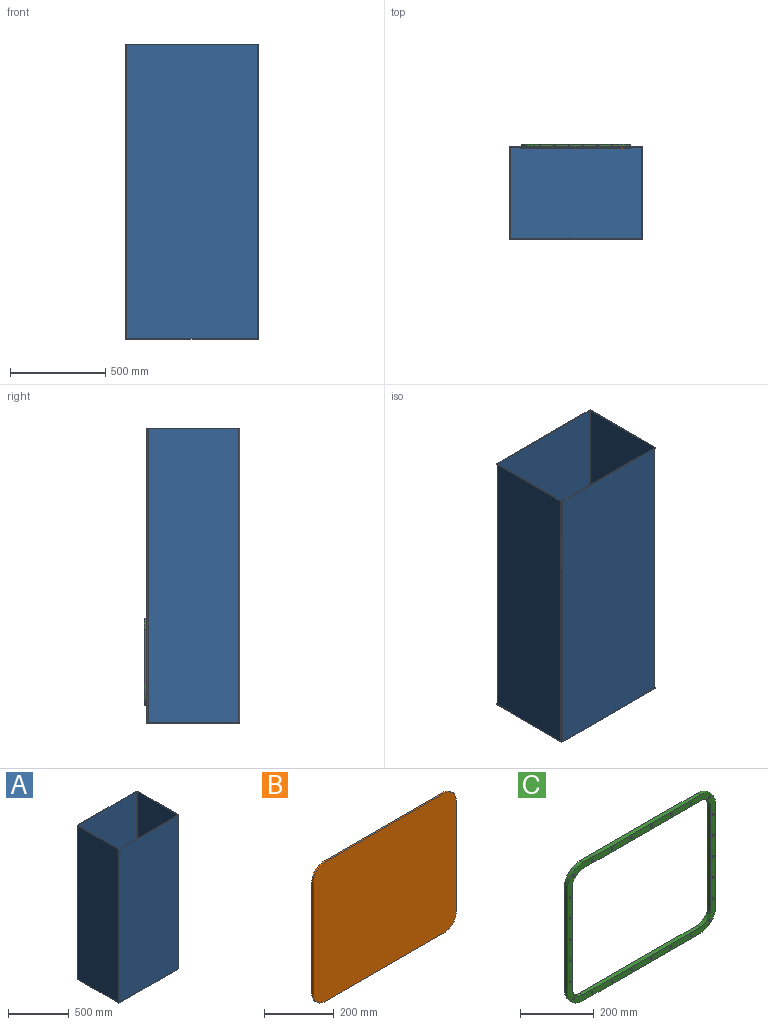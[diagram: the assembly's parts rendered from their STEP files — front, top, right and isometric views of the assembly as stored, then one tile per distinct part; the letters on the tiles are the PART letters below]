
ASSEMBLY  parts=3 mates=3
PART A: 35 faces, bbox 701.3x491.3x1550 mm
  f0: plane 1547x474mm, normal (1,0,0), area 733278mm2, adj f1,f15,f16,f19
  f1: cylinder r=8mm len=1547mm, axis (0,0,-1), area 19440.2mm2, adj f0,f2,f16,f21
  f2: plane 1547x684mm, normal (0,1,0), area 815920.6mm2, adj f1,f3,f16,f23,f27,f28,f29,f30
  f3: cylinder r=8mm len=1547mm, axis (0,0,-1), area 19440.2mm2, adj f2,f4,f16,f25
  f4: plane 1547x474mm, normal (-1,0,0), area 733278mm2, adj f3,f5,f16,f26
  f5: cylinder r=8mm len=1547mm, axis (0,0,-1), area 19440.2mm2, adj f4,f6,f16,f24
  f6: plane 1547x684mm, normal (0,-1,0), area 1058148mm2, adj f5,f15,f16,f22
  f7: cylinder r=4mm len=1538mm, axis (0,0,-1), area 9663.5mm2, adj f8,f14,f16,f18
  f8: plane 1538x472mm, normal (-1,0,0), area 725936mm2, adj f7,f9,f16,f18
  f9: cylinder r=4mm len=1538mm, axis (0,0,-1), area 9663.5mm2, adj f8,f10,f16,f18
  f10: plane 1538x682mm, normal (0,1,0), area 1048916mm2, adj f9,f11,f16,f18
  f11: cylinder r=4mm len=1538mm, axis (0,0,-1), area 9663.5mm2, adj f10,f12,f16,f18
  f12: plane 1538x472mm, normal (1,0,0), area 725936mm2, adj f11,f13,f16,f18
  f13: cylinder r=4mm len=1538mm, axis (0,0,-1), area 9663.5mm2, adj f12,f14,f16,f18
  f14: plane 1538x682mm, normal (0,-1,0), area 806688.6mm2, adj f7,f13,f16,f18,f27,f28,f29,f30
  f15: cylinder r=8mm len=1547mm, axis (0,0,-1), area 19440.2mm2, adj f0,f6,f16,f20
  f16: plane 700x490mm, normal (0,0,1), area 11758.8mm2, adj f0,f1,f2,f3,f4,f5,f6,f7
  f17: plane 694x484mm, normal (0,0,-1), area 335874.5mm2, adj f19,f20,f21,f22,f23,f24,f25,f26
  f18: plane 690x480mm, normal (0,0,1), area 331186.3mm2, adj f7,f8,f9,f10,f11,f12,f13,f14
  f19: cylinder r=3mm len=474mm, axis (0,1,0), area 2233.7mm2, adj f0,f17,f20,f21
  f20: torus R=5mm, axis (0,0,1), area 51.1mm2, adj f15,f17,f19,f22
  f21: torus R=5mm, axis (0,0,1), area 51.1mm2, adj f1,f17,f19,f23
  f22: cylinder r=3mm len=684mm, axis (1,0,0), area 3223.3mm2, adj f6,f17,f20,f24
  f23: cylinder r=3mm len=684mm, axis (-1,0,0), area 3223.3mm2, adj f2,f17,f21,f25
  f24: torus R=5mm, axis (0,0,1), area 51.1mm2, adj f5,f17,f22,f26
  f25: torus R=5mm, axis (0,0,1), area 51.1mm2, adj f3,f17,f23,f26
  f26: cylinder r=3mm len=474mm, axis (0,-1,0), area 2233.7mm2, adj f4,f17,f24,f25
  f27: plane 390x5mm, normal (1,0,0), area 1950mm2, adj f2,f14,f28,f34
  f28: cylinder r=30mm len=30mm, axis (0,1,0), area 235.6mm2, adj f2,f14,f27,f29
  f29: plane 480x5mm, normal (0,0,-1), area 2400mm2, adj f2,f14,f28,f30
  f30: cylinder r=30mm len=30mm, axis (0,1,0), area 235.6mm2, adj f2,f14,f29,f31
  f31: plane 390x5mm, normal (-1,0,0), area 1950mm2, adj f2,f14,f30,f32
  f32: cylinder r=30mm len=30mm, axis (0,1,0), area 235.6mm2, adj f2,f14,f31,f33
  f33: plane 480x5mm, normal (0,0,1), area 2400mm2, adj f2,f14,f32,f34
  f34: cylinder r=30mm len=30mm, axis (0,1,0), area 235.6mm2, adj f2,f14,f27,f33
PART B: 10 faces, bbox 580x6x490 mm
  f0: plane 390x6mm, normal (-1,0,0), area 2340mm2, adj f1,f7,f8,f9
  f1: cylinder r=50mm len=50mm, axis (0,1,0), area 471.2mm2, adj f0,f2,f8,f9
  f2: plane 480x6mm, normal (0,0,1), area 2880mm2, adj f1,f3,f8,f9
  f3: cylinder r=50mm len=50mm, axis (0,1,0), area 471.2mm2, adj f2,f4,f8,f9
  f4: plane 390x6mm, normal (1,0,0), area 2340mm2, adj f3,f5,f8,f9
  f5: cylinder r=50mm len=50mm, axis (0,1,0), area 471.2mm2, adj f4,f6,f8,f9
  f6: plane 480x6mm, normal (0,0,-1), area 2880mm2, adj f5,f7,f8,f9
  f7: cylinder r=50mm len=50mm, axis (0,1,0), area 471.2mm2, adj f0,f6,f8,f9
  f8: plane 580x490mm, normal (0,-1,0), area 282054mm2, adj f0,f1,f2,f3,f4,f5,f6,f7
  f9: plane 580x490mm, normal (0,1,0), area 282054mm2, adj f0,f1,f2,f3,f4,f5,f6,f7
PART C: 96 faces, bbox 570x12x460 mm
  f0: plane 340x12mm, normal (1,0,0), area 4080mm2, adj f1,f15,f16,f17
  f1: cylinder r=60mm len=60mm, axis (0,1,0), area 1131mm2, adj f0,f2,f16,f17
  f2: plane 450x12mm, normal (0,0,1), area 5400mm2, adj f1,f3,f16,f17
  f3: cylinder r=60mm len=60mm, axis (0,1,0), area 1131mm2, adj f2,f4,f16,f17
  f4: plane 340x12mm, normal (-1,0,0), area 4080mm2, adj f3,f5,f16,f17
  f5: cylinder r=60mm len=60mm, axis (0,1,0), area 1131mm2, adj f4,f6,f16,f17
  f6: plane 450x12mm, normal (0,0,-1), area 5400mm2, adj f5,f15,f16,f17
  f7: cylinder r=40mm len=40mm, axis (0,1,0), area 754mm2, adj f8,f14,f16,f17
  f8: plane 340x12mm, normal (-1,0,0), area 4080mm2, adj f7,f9,f16,f17
  f9: cylinder r=40mm len=40mm, axis (0,1,0), area 754mm2, adj f8,f10,f16,f17
  f10: plane 450x12mm, normal (0,0,1), area 5400mm2, adj f9,f11,f16,f17
  f11: cylinder r=40mm len=40mm, axis (0,1,0), area 754mm2, adj f10,f12,f16,f17
  f12: plane 340x12mm, normal (1,0,0), area 4080mm2, adj f11,f13,f16,f17
  f13: cylinder r=40mm len=40mm, axis (0,1,0), area 754mm2, adj f12,f14,f16,f17
  f14: plane 450x12mm, normal (0,0,-1), area 5400mm2, adj f7,f13,f16,f17
  f15: cylinder r=60mm len=60mm, axis (0,1,0), area 1131mm2, adj f0,f6,f16,f17
  f16: plane 570x460mm, normal (0,-1,0), area 36993.7mm2, adj f0,f1,f2,f3,f4,f5,f6,f7
  f17: plane 570x460mm, normal (0,1,0), area 35298.7mm2, adj f0,f1,f2,f3,f4,f5,f6,f7
  f18: cylinder r=3.3mm len=6.6mm, axis (0,1,0), area 124.4mm2, adj f16,f19
  f19: plane 11.25x11.25mm, normal (0,1,0), area 65.2mm2, adj f18,f20
  f20: cylinder r=5.62mm len=11.25mm, axis (0,1,0), area 212.1mm2, adj f17,f19
  f21: cylinder r=3.3mm len=6.6mm, axis (0,1,0), area 124.4mm2, adj f16,f22
  f22: plane 11.25x11.25mm, normal (0,1,0), area 65.2mm2, adj f21,f23
  f23: cylinder r=5.62mm len=11.25mm, axis (0,1,0), area 212.1mm2, adj f17,f22
  f24: cylinder r=3.3mm len=6.6mm, axis (0,1,0), area 124.4mm2, adj f16,f25
  f25: plane 11.25x11.25mm, normal (0,1,0), area 65.2mm2, adj f24,f26
  f26: cylinder r=5.62mm len=11.25mm, axis (0,1,0), area 212.1mm2, adj f17,f25
  f27: cylinder r=3.3mm len=6.6mm, axis (0,1,0), area 124.4mm2, adj f16,f28
  f28: plane 11.25x11.25mm, normal (0,1,0), area 65.2mm2, adj f27,f29
  f29: cylinder r=5.62mm len=11.25mm, axis (0,1,0), area 212.1mm2, adj f17,f28
  f30: cylinder r=3.3mm len=6.6mm, axis (0,1,0), area 124.4mm2, adj f16,f31
  f31: plane 11.25x11.25mm, normal (0,1,0), area 65.2mm2, adj f30,f32
  f32: cylinder r=5.62mm len=11.25mm, axis (0,1,0), area 212.1mm2, adj f17,f31
  f33: cylinder r=3.3mm len=6.6mm, axis (0,1,0), area 124.4mm2, adj f16,f34
  f34: plane 11.25x11.25mm, normal (0,1,0), area 65.2mm2, adj f33,f35
  f35: cylinder r=5.62mm len=11.25mm, axis (0,1,0), area 212.1mm2, adj f17,f34
  f36: cylinder r=3.3mm len=6.6mm, axis (0,1,0), area 124.4mm2, adj f16,f37
  f37: plane 11.25x11.25mm, normal (0,1,0), area 65.2mm2, adj f36,f38
  f38: cylinder r=5.62mm len=11.25mm, axis (0,1,0), area 212.1mm2, adj f17,f37
  f39: cylinder r=3.3mm len=6.6mm, axis (0,1,0), area 124.4mm2, adj f16,f40
  f40: plane 11.25x11.25mm, normal (0,1,0), area 65.2mm2, adj f39,f41
  f41: cylinder r=5.62mm len=11.25mm, axis (0,1,0), area 212.1mm2, adj f17,f40
  f42: cylinder r=3.3mm len=6.6mm, axis (0,1,0), area 124.4mm2, adj f16,f43
  f43: plane 11.25x11.25mm, normal (0,1,0), area 65.2mm2, adj f42,f44
  f44: cylinder r=5.62mm len=11.25mm, axis (0,1,0), area 212.1mm2, adj f17,f43
  f45: cylinder r=3.3mm len=6.6mm, axis (0,1,0), area 124.4mm2, adj f16,f46
  f46: plane 11.25x11.25mm, normal (0,1,0), area 65.2mm2, adj f45,f47
  f47: cylinder r=5.62mm len=11.25mm, axis (0,1,0), area 212.1mm2, adj f17,f46
  f48: cylinder r=3.3mm len=6.6mm, axis (0,1,0), area 124.4mm2, adj f16,f49
  f49: plane 11.25x11.25mm, normal (0,1,0), area 65.2mm2, adj f48,f50
  f50: cylinder r=5.62mm len=11.25mm, axis (0,1,0), area 212.1mm2, adj f17,f49
  f51: cylinder r=3.3mm len=6.6mm, axis (0,1,0), area 124.4mm2, adj f16,f52
  f52: plane 11.25x11.25mm, normal (0,1,0), area 65.2mm2, adj f51,f53
  f53: cylinder r=5.62mm len=11.25mm, axis (0,1,0), area 212.1mm2, adj f17,f52
  f54: cylinder r=3.3mm len=6.6mm, axis (0,1,0), area 124.4mm2, adj f16,f55
  f55: plane 11.25x11.25mm, normal (0,1,0), area 65.2mm2, adj f54,f56
  f56: cylinder r=5.62mm len=11.25mm, axis (0,1,0), area 212.1mm2, adj f17,f55
  f57: cylinder r=3.3mm len=6.6mm, axis (0,1,0), area 124.4mm2, adj f16,f58
  f58: plane 11.25x11.25mm, normal (0,1,0), area 65.2mm2, adj f57,f59
  f59: cylinder r=5.62mm len=11.25mm, axis (0,1,0), area 212.1mm2, adj f17,f58
  f60: cylinder r=3.3mm len=6.6mm, axis (0,1,0), area 124.4mm2, adj f16,f61
  f61: plane 11.25x11.25mm, normal (0,1,0), area 65.2mm2, adj f60,f62
  f62: cylinder r=5.62mm len=11.25mm, axis (0,1,0), area 212.1mm2, adj f17,f61
  f63: cylinder r=3.3mm len=6.6mm, axis (0,1,0), area 124.4mm2, adj f16,f64
  f64: plane 11.25x11.25mm, normal (0,1,0), area 65.2mm2, adj f63,f65
  f65: cylinder r=5.62mm len=11.25mm, axis (0,1,0), area 212.1mm2, adj f17,f64
  f66: cylinder r=3.3mm len=6.6mm, axis (0,1,0), area 124.4mm2, adj f16,f67
  f67: plane 11.25x11.25mm, normal (0,1,0), area 65.2mm2, adj f66,f68
  f68: cylinder r=5.62mm len=11.25mm, axis (0,1,0), area 212.1mm2, adj f17,f67
  f69: cylinder r=3.3mm len=6.6mm, axis (0,1,0), area 124.4mm2, adj f16,f70
  f70: plane 11.25x11.25mm, normal (0,1,0), area 65.2mm2, adj f69,f71
  f71: cylinder r=5.62mm len=11.25mm, axis (0,1,0), area 212.1mm2, adj f17,f70
  f72: cylinder r=3.3mm len=6.6mm, axis (0,1,0), area 124.4mm2, adj f16,f73
  f73: plane 11.25x11.25mm, normal (0,1,0), area 65.2mm2, adj f72,f74
  f74: cylinder r=5.62mm len=11.25mm, axis (0,1,0), area 212.1mm2, adj f17,f73
  f75: cylinder r=3.3mm len=6.6mm, axis (0,1,0), area 124.4mm2, adj f16,f76
  f76: plane 11.25x11.25mm, normal (0,1,0), area 65.2mm2, adj f75,f77
  f77: cylinder r=5.62mm len=11.25mm, axis (0,1,0), area 212.1mm2, adj f17,f76
  f78: cylinder r=3.3mm len=6.6mm, axis (0,1,0), area 124.4mm2, adj f16,f79
  f79: plane 11.25x11.25mm, normal (0,1,0), area 65.2mm2, adj f78,f80
  f80: cylinder r=5.62mm len=11.25mm, axis (0,1,0), area 212.1mm2, adj f17,f79
  f81: cylinder r=3.3mm len=6.6mm, axis (0,1,0), area 124.4mm2, adj f16,f82
  f82: plane 11.25x11.25mm, normal (0,1,0), area 65.2mm2, adj f81,f83
  f83: cylinder r=5.62mm len=11.25mm, axis (0,1,0), area 212.1mm2, adj f17,f82
  f84: cylinder r=3.3mm len=6.6mm, axis (0,1,0), area 124.4mm2, adj f16,f85
  f85: plane 11.25x11.25mm, normal (0,1,0), area 65.2mm2, adj f84,f86
  f86: cylinder r=5.62mm len=11.25mm, axis (0,1,0), area 212.1mm2, adj f17,f85
  f87: cylinder r=3.3mm len=6.6mm, axis (0,1,0), area 124.4mm2, adj f16,f88
  f88: plane 11.25x11.25mm, normal (0,1,0), area 65.2mm2, adj f87,f89
  f89: cylinder r=5.62mm len=11.25mm, axis (0,1,0), area 212.1mm2, adj f17,f88
  f90: cylinder r=3.3mm len=6.6mm, axis (0,1,0), area 124.4mm2, adj f16,f91
  f91: plane 11.25x11.25mm, normal (0,1,0), area 65.2mm2, adj f90,f92
  f92: cylinder r=5.62mm len=11.25mm, axis (0,1,0), area 212.1mm2, adj f17,f91
  f93: cylinder r=3.3mm len=6.6mm, axis (0,1,0), area 124.4mm2, adj f16,f94
  f94: plane 11.25x11.25mm, normal (0,1,0), area 65.2mm2, adj f93,f95
  f95: cylinder r=5.62mm len=11.25mm, axis (0,1,0), area 212.1mm2, adj f17,f94
PLACE A t=(245.15,-194.24,46.54)mm fixed
PLACE B t=(240.97,-193.24,44.7)mm
PLACE C t=(244.99,62.76,370.45)mm
MATE parallel C.f6 <-> A.f17  axis (0,0,-1) through (244.99,56.76,140.45)mm
MATE planar C.f16 <-> A.f2  axis (0,-1,0) through (244.99,50.76,370.45)mm
MATE planar B.f9 <-> A.f14  axis (0,1,0) through (240.97,45.76,369.7)mm
